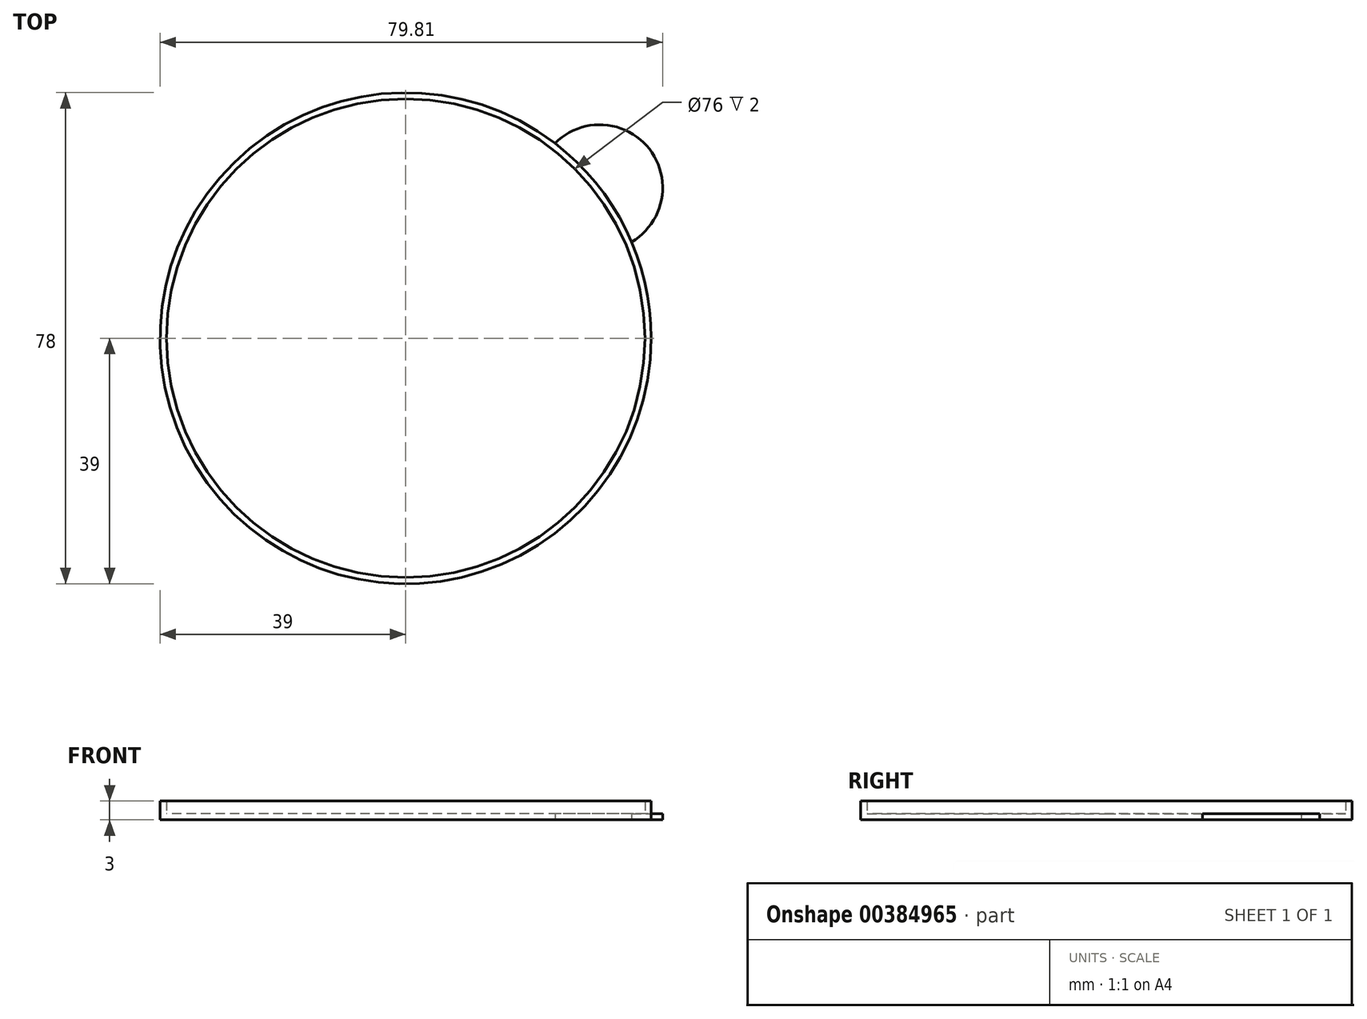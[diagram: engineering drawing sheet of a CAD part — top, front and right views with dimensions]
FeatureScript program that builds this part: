
annotation { "Feature Type Name" : "Feature", "Feature Type Description" : "" }
export const myFeature = defineFeature(function(context is Context, id is Id, definition is map)
    precondition{}
    {
        {
            var Q0;
            Q0=qCreatedBy(makeId("Top.planeOp"),FACE);
            var sketch = newSketch(context, id + "F0", { "sketchPlane" : qUnion([Q0])});
            skCircle(sketch, "E0", {"center": v(0, 0) * mm, "radius": 38 * mm});
            skSolve(sketch);
        }
        {
            var Q0;
            Q0 = qSketchRegion(id + "F0", true);
            var sketch = newSketch(context, id + "F1", { "sketchPlane" : qUnion([Q0])});
            skCircle(sketch, "E1", {"center": v(0, 0) * mm, "radius": 39 * mm});
            skSolve(sketch);
        }
        {
            var Q0;
            Q0=makeQuery(id+"F0.imprint","IMPRINT",FACE,{"disambiguationData":[TD([[makeQuery(id+"F0.imprint","IMPRINT",EDGE,{"derivedFrom":sQuery(id+"F0.wireOp",EDGE,"E0")}),1.0]])]});
            extrude(context, id + "F2", {"entities" : qUnion([Q0]), "depth" : 1 * mm});
        }
        {
            var Q0;
            Q0=makeQuery(id+"F1.imprint","IMPRINT",FACE,{"disambiguationData":[TD([[makeQuery(id+"F1.imprint","IMPRINT",EDGE,{"derivedFrom":sQuery(id+"F1.wireOp",EDGE,"E1")}),1.0]])]});
            extrude(context, id + "F3", {"entities" : qUnion([Q0]), "operationType" : NewBodyOperationType.ADD, "depth" : 3 * mm});
        }
        {
            var Q0;
            Q0=makeQuery(id+"F0.imprint","IMPRINT",FACE,{"disambiguationData":[TD([[makeQuery(id+"F0.imprint","IMPRINT",EDGE,{"derivedFrom":sQuery(id+"F0.wireOp",EDGE,"E0")}),1.0]])]});
            var sketch = newSketch(context, id + "F4", { "sketchPlane" : qUnion([Q0])});
            skCircle(sketch, "E2", {"center": v(30.8, 23.91) * mm, "radius": 10 * mm});
            skSolve(sketch);
        }
        {
            var Q0;
            {var subQ0=sQuery(id+"F4.wireOp",EDGE,"E2");var subQ1=makeQuery(id+"F0.imprint","IMPRINT",EDGE,{"derivedFrom":sQuery(id+"F0.wireOp",EDGE,"E0")});var subQ2=makeQuery(id+"F4.imprint","INTERSECT",VERTEX,{"disambiguationData":[OD(0.0)],"derivedFrom":[subQ1,subQ0]});Q0=makeQuery(id+"F4.imprint","IMPRINT",FACE,{"disambiguationData":[TD([[makeQuery(id+"F4.imprint","IMPRINT",EDGE,{"disambiguationData":[TD([[subQ2,1.0]])],"derivedFrom":subQ0}),1.0]])]});}
            extrude(context, id + "F5", {"entities" : qUnion([Q0]), "operationType" : NewBodyOperationType.ADD, "depth" : 1 * mm});
        }
    });
